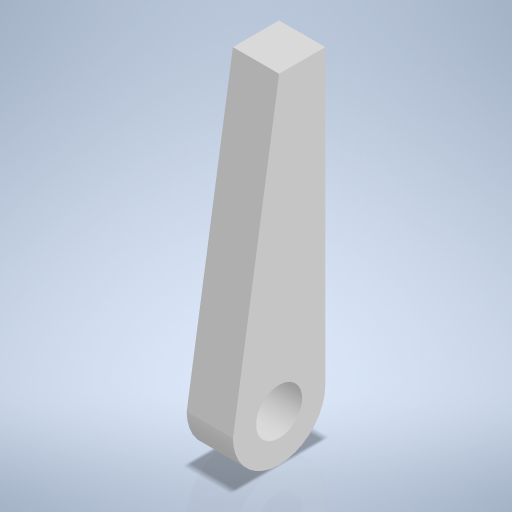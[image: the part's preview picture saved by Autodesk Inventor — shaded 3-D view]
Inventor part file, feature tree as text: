
AUTODESK INVENTOR PART (.ipt)
format: ipt  version: 2024 (Build 280153000, 153)  size: 233,472 bytes
history: native  units: mm
features: sketch x2, extrude x1, hole x1
ambient origin geometry x8: Origin, YZ Plane, XZ Plane, XY Plane, X Axis, Y Axis, Z Axis, Center Point
bodies: Volumenkörper1 (feature_tree)
feature tree (4):
  extrude  "Extrusion1"  Depth=19.0mm
  hole  "Bohrung1"  [1 undecoded]
  sketch  "Skizze1"  dims[d0=3.0mm d1=19.0mm]
  sketch  "Skizze2"  dims[d2=3.0mm d3=3.0mm d4=3.0mm d5=0.0mm d6=3.0mm d7=6.0mm d8=4.0mm d9=2.0mm d10=90.0deg d11=8.0mm d12=0.0mm]
note: 1 required parameter value undecoded (feature->parameter linkage not recoverable at this tier; creation-order binding heuristic only, values carry confidence <= 0.55)
